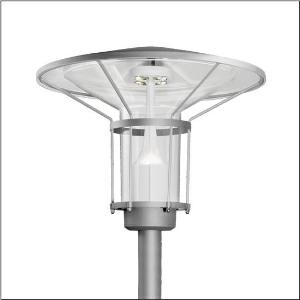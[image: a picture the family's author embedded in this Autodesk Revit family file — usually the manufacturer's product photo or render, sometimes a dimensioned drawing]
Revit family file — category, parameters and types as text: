
# Revit family: laterne_classic_iq___pl1_2s_5xa5245cf14h_6b83
name_source: partatom
category: Lighting Fixtures
units: mm (PartAtom-declared; Revit-internal decimal feet)

## family parameters
Cut with Voids When Loaded = No
Host = Face
Light Source = No
Part Type = Normal
Room Calculation Point = No
Round Connector Dimension = Use Diameter
Shared = No

## types (1)
- --- (1 x LED, 2670 lm, 23.9 W, 2200K)
    Apparent Load = 24 VA
    CIE Flux Codes = 21 60 93 97 100
    Color Rendering = 70
    Color Temperature = 2200K
    Default Elevation = 1800 mm
    Description = Lantern Classic iQ, mast luminaire, Module 540 iQ-SR, primary light control with 3 zone facetted reflector, of plastic, silver coated, highly specular, structured, primary optical cover: cover, of PMMA, transparent, light distribution: PL1.2s, light emission: direct distribution, primary light characteristic: symmetric, installation type: post-top, LED, High Power LED, rated luminous flux: 2.670lm, luminous efficacy: 112lm/W, light colour: 722, colour temperature: 2200K, control gear: ECG iQ, control: presetting dimming logarithmic, Street-Remote, Auto-Match, Temp-Guard, Lumen-Switch, Night-Set, Smart-Wire, Light-Fading, Desk-Remote (wireless, voltage-free reading and setting of iQ features in the workshop via application-optimized NFC function/RFID function), optimised constant luminous flux control (CLO 2.0), with terminal, 6-pole, max. 2.5mm², mains connection: 230..240V, AC, 50/60Hz, start of lifetime: 24W, end of service life: 26W, reduction: 12W, luminaire housing, upper part, of glass-fibre reinforced polyester, coated, Siteco® metallic grey (DB 702S), diameter: 750mm, height: 596mm, spigot size: d x l = 76 x 70mm (post-top) | with reducer (optional accessory) 60 x 70mm, post-top mast mounting element, of diecast aluminium, coated, Siteco® metallic grey (DB 702S), Module 540 iQ-SR, traffic white (RAL 9016), equipment: standard, protection rating (complete): IP65, insulation class (complete): insulation class II (safety insulation), certification: CE, ENEC, VDE, packaging unit: 1 piece

Light Distribution: PL1.2s
    Height = 596 mm
    Lamp = 1 x LED
    Lamp Light Flux = 2670 lm
    Lamp Power = 23.9 W
    Lamp count = 1
    Length = 750 mm
    Luminous efficacy = 112 lm/W
    Manufacturer = Siteco
    ModVariant = No
    Model = 5XA5245CF14H
    Number of Poles = 1
    OnlyDefault = Yes
    Power Factor = 1
    Product Name = Laterne Classic iQ | PL1.2s
    Product group = mast luminaire | pylon top
    ProductGroupID = 6100
    Protection Class = Protection class II
    Protection Degree = IP 65
    RLX_Detail_Level = 1
    RLX_Emergency_Light_Flux = 0 lm
    RLX_Emergency_Type = 0
    RLX_Emergency_Type_DB = No
    RlxData = <blob elided: 62777 chars, md5=ed46d3bc>
    Socket = socket
    Standby Power = 0 W
    System Light Flux = 2670 lm
    System Power = 24 W
    Type Comments = factory setting: luminous flux: 100 % | dim-lin: 254 | 499 mA
    Type Image = l_1006052.jpg
    URL = http://relux.com
    VarID = @adj_095343
    Voltage = 0 V
    Weight = 0.00 kg
    Width = 0 mm  [stored 0 ft]

note: [stored X ft] marks values corroborated as IEEE doubles in the binary element streams (Revit-internal decimal feet)

## geometry (parser evidence)
native form markers: Blend x4, Sweep x10
no freeform markers — native parametric forms only
